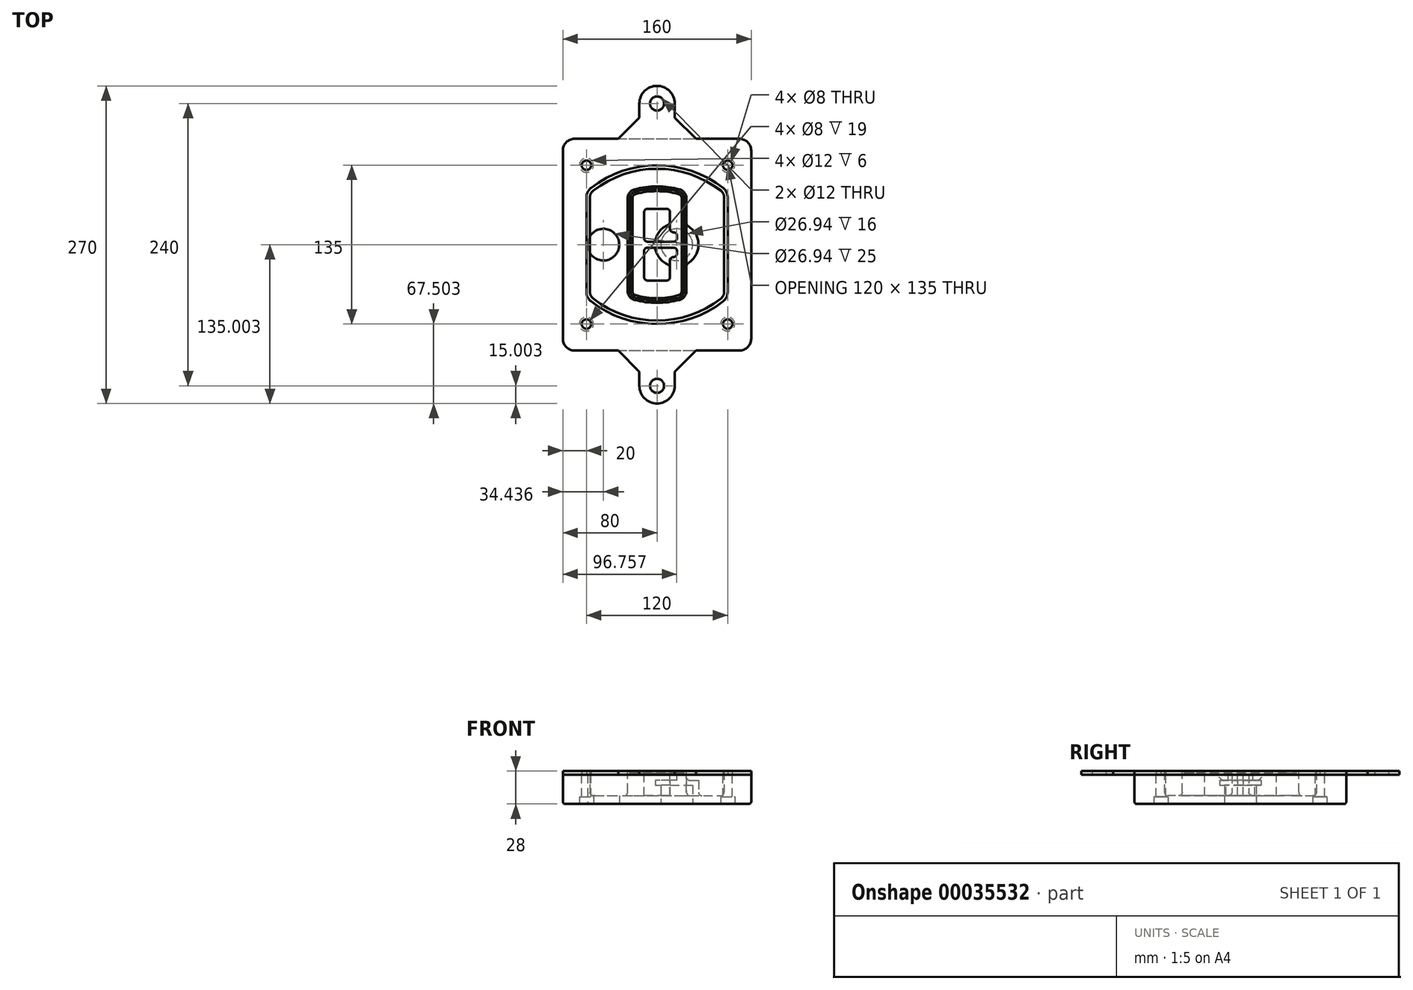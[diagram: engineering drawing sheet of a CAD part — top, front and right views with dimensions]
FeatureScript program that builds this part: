
annotation { "Feature Type Name" : "Feature", "Feature Type Description" : "" }
export const myFeature = defineFeature(function(context is Context, id is Id, definition is map)
    precondition{}
    {
        {
            var Q0;
            Q0=qCreatedBy(makeId("Top.planeOp"),FACE);
            var sketch = newSketch(context, id + "F0", { "sketchPlane" : qUnion([Q0])});
            skPoint(sketch, "E0.rect.middle", {"position": v(0, 0) * mm});
            skLineSegment(sketch, "E1.bottom", {"start": v(24.05, 28.38) * mm, "end": v(164.05, 28.38) * mm});
            skLineSegment(sketch, "E1.top", {"start": v(24.05, 208.38) * mm, "end": v(164.05, 208.38) * mm});
            skLineSegment(sketch, "E1.left", {"start": v(14.05, 38.38) * mm, "end": v(14.05, 198.38) * mm});
            skLineSegment(sketch, "E1.right", {"start": v(174.05, 38.38) * mm, "end": v(174.05, 198.38) * mm});
            skLineSegment(sketch, "E2", {"start": v(14.05, 208.38) * mm, "end": v(174.05, 28.38) * mm, "construction": true});
            skLineSegment(sketch, "E3", {"start": v(174.05, 208.38) * mm, "end": v(14.05, 28.38) * mm, "construction": true});
            skCircle(sketch, "E4", {"center": v(34.05, 185.88) * mm, "radius": 4 * mm});
            skCircle(sketch, "E5", {"center": v(154.05, 185.88) * mm, "radius": 4 * mm});
            skCircle(sketch, "E6", {"center": v(154.05, 50.88) * mm, "radius": 4 * mm});
            skCircle(sketch, "E7", {"center": v(34.05, 50.88) * mm, "radius": 4 * mm});
            skLineSegment(sketch, "E8", {"start": v(34.05, 185.88) * mm, "end": v(154.05, 185.88) * mm, "construction": true});
            skLineSegment(sketch, "E9", {"start": v(154.05, 185.88) * mm, "end": v(154.05, 50.88) * mm, "construction": true});
            skLineSegment(sketch, "E10", {"start": v(154.05, 50.88) * mm, "end": v(34.05, 50.88) * mm, "construction": true});
            skLineSegment(sketch, "E11", {"start": v(34.05, 50.88) * mm, "end": v(34.05, 185.88) * mm, "construction": true});
            skLineSegment(sketch, "E12", {"start": v(34.05, 158.68) * mm, "end": v(34.05, 78.09) * mm});
            skLineSegment(sketch, "E13", {"start": v(154.05, 158.68) * mm, "end": v(154.05, 78.09) * mm});
            skArc(sketch, "E14", {"start": v(150.2, 166.56) * mm, "mid": v(94.05, 185.88) * mm, "end": v(37.9, 166.56) * mm});
            skArc(sketch, "E15", {"start": v(37.9, 70.2) * mm, "mid": v(94.05, 50.88) * mm, "end": v(150.2, 70.2) * mm});
            skLineSegment(sketch, "E16", {"start": v(34.05, 118.38) * mm, "end": v(154.05, 118.38) * mm, "construction": true});
            skPoint(sketch, "E17.visualSharp", {"position": v(34.05, 73.38) * mm});
            skArc(sketch, "E17.filletArc", {"start": v(34.05, 78.09) * mm, "mid": v(35.06, 73.7) * mm, "end": v(37.9, 70.2) * mm});
            skPoint(sketch, "E18.visualSharp", {"position": v(34.05, 163.38) * mm});
            skArc(sketch, "E18.filletArc", {"start": v(37.9, 166.56) * mm, "mid": v(35.06, 163.06) * mm, "end": v(34.05, 158.68) * mm});
            skPoint(sketch, "E19.visualSharp", {"position": v(154.05, 163.38) * mm});
            skArc(sketch, "E19.filletArc", {"start": v(154.05, 158.68) * mm, "mid": v(153.04, 163.06) * mm, "end": v(150.2, 166.56) * mm});
            skPoint(sketch, "E20.visualSharp", {"position": v(154.05, 73.38) * mm});
            skArc(sketch, "E20.filletArc", {"start": v(150.2, 70.2) * mm, "mid": v(153.04, 73.7) * mm, "end": v(154.05, 78.09) * mm});
            skPoint(sketch, "E21.visualSharp", {"position": v(14.05, 208.38) * mm});
            skArc(sketch, "E21.filletArc", {"start": v(24.05, 208.38) * mm, "mid": v(16.98, 205.45) * mm, "end": v(14.05, 198.38) * mm});
            skPoint(sketch, "E22.visualSharp", {"position": v(174.05, 208.38) * mm});
            skArc(sketch, "E22.filletArc", {"start": v(174.05, 198.38) * mm, "mid": v(171.12, 205.45) * mm, "end": v(164.05, 208.38) * mm});
            skPoint(sketch, "E23.visualSharp", {"position": v(174.05, 28.38) * mm});
            skArc(sketch, "E23.filletArc", {"start": v(164.05, 28.38) * mm, "mid": v(171.12, 31.31) * mm, "end": v(174.05, 38.38) * mm});
            skPoint(sketch, "E24.visualSharp", {"position": v(14.05, 28.38) * mm});
            skArc(sketch, "E24.filletArc", {"start": v(14.05, 38.38) * mm, "mid": v(16.98, 31.31) * mm, "end": v(24.05, 28.38) * mm});
            skArc(sketch, "E25.0", {"start": v(151.05, 158.68) * mm, "mid": v(150.34, 161.75) * mm, "end": v(148.36, 164.2) * mm});
            skLineSegment(sketch, "E25.1", {"start": v(151.05, 158.68) * mm, "end": v(151.05, 78.09) * mm});
            skArc(sketch, "E25.2", {"start": v(148.36, 72.57) * mm, "mid": v(150.34, 75.02) * mm, "end": v(151.05, 78.09) * mm});
            skArc(sketch, "E25.3", {"start": v(39.74, 72.57) * mm, "mid": v(94.05, 53.88) * mm, "end": v(148.36, 72.57) * mm});
            skArc(sketch, "E25.4", {"start": v(37.05, 78.09) * mm, "mid": v(37.76, 75.02) * mm, "end": v(39.74, 72.57) * mm});
            skArc(sketch, "E25.5", {"start": v(148.36, 164.2) * mm, "mid": v(94.05, 182.88) * mm, "end": v(39.74, 164.2) * mm});
            skLineSegment(sketch, "E25.6", {"start": v(37.05, 158.68) * mm, "end": v(37.05, 78.09) * mm});
            skArc(sketch, "E25.7", {"start": v(39.74, 164.2) * mm, "mid": v(37.76, 161.75) * mm, "end": v(37.05, 158.68) * mm});
            skArc(sketch, "E26.0", {"start": v(35.43, 169.71) * mm, "mid": v(31.47, 164.82) * mm, "end": v(30.05, 158.68) * mm});
            skArc(sketch, "E26.1", {"start": v(152.67, 169.71) * mm, "mid": v(94.05, 189.88) * mm, "end": v(35.43, 169.71) * mm});
            skArc(sketch, "E26.2", {"start": v(158.05, 158.68) * mm, "mid": v(156.63, 164.82) * mm, "end": v(152.67, 169.71) * mm});
            skLineSegment(sketch, "E26.3", {"start": v(158.05, 158.68) * mm, "end": v(158.05, 78.09) * mm});
            skArc(sketch, "E26.4", {"start": v(152.67, 67.05) * mm, "mid": v(156.63, 71.95) * mm, "end": v(158.05, 78.09) * mm});
            skLineSegment(sketch, "E26.5", {"start": v(30.05, 158.68) * mm, "end": v(30.05, 78.09) * mm});
            skArc(sketch, "E26.6", {"start": v(35.43, 67.05) * mm, "mid": v(94.05, 46.88) * mm, "end": v(152.67, 67.05) * mm});
            skArc(sketch, "E26.7", {"start": v(30.05, 78.09) * mm, "mid": v(31.47, 71.95) * mm, "end": v(35.43, 67.05) * mm});
            skSolve(sketch);
        }
        {
            var Q0;
            Q0=makeQuery(id+"F0.imprint","IMPRINT",FACE,{"disambiguationData":[TD([[makeQuery(id+"F0.imprint","IMPRINT",EDGE,{"derivedFrom":sQuery(id+"F0.wireOp",EDGE,"E1.bottom")}),1.0]])]});
            var Q1;
            Q1=makeQuery(id+"F0.imprint","IMPRINT",FACE,{"disambiguationData":[TD([[makeQuery(id+"F0.imprint","IMPRINT",EDGE,{"derivedFrom":sQuery(id+"F0.wireOp",EDGE,"E12")}),1.0]])]});
            var Q2;
            Q2=makeQuery(id+"F0.imprint","IMPRINT",FACE,{"disambiguationData":[TD([[makeQuery(id+"F0.imprint","IMPRINT",EDGE,{"derivedFrom":sQuery(id+"F0.wireOp",EDGE,"E25.0")}),1.0]])]});
            var Q3;
            Q3=makeQuery(id+"F0.imprint","IMPRINT",FACE,{"disambiguationData":[TD([[makeQuery(id+"F0.imprint","IMPRINT",EDGE,{"derivedFrom":sQuery(id+"F0.wireOp",EDGE,"E12")}),-1.0]])]});
            extrude(context, id + "F1", {"entities" : qUnion([Q0, Q1, Q2, Q3]), "oppositeDirection" : true, "depth" : 25 * mm});
        }
        {
            var Q0;
            Q0=makeQuery(id+"F0.imprint","IMPRINT",FACE,{"disambiguationData":[TD([[makeQuery(id+"F0.imprint","IMPRINT",EDGE,{"derivedFrom":sQuery(id+"F0.wireOp",EDGE,"E12")}),1.0]])]});
            extrude(context, id + "F2", {"entities" : qUnion([Q0]), "operationType" : NewBodyOperationType.ADD, "depth" : 3 * mm});
        }
        {
            var Q0;
            Q0=makeQuery(id+"F0.imprint","IMPRINT",FACE,{"disambiguationData":[TD([[makeQuery(id+"F0.imprint","IMPRINT",EDGE,{"derivedFrom":sQuery(id+"F0.wireOp",EDGE,"E25.0")}),1.0]])]});
            extrude(context, id + "F3", {"entities" : qUnion([Q0]), "operationType" : NewBodyOperationType.REMOVE, "oppositeDirection" : true, "depth" : 18 * mm});
        }
        {
            var Q0;
            Q0=makeQuery(id+"F2.opExtrude","CAP_FACE",FACE,{"disambiguationData":[OSD([sQuery(id+"F0.wireOp",EDGE,"E12"),sQuery(id+"F0.wireOp",EDGE,"E13"),sQuery(id+"F0.wireOp",EDGE,"E14"),sQuery(id+"F0.wireOp",EDGE,"E15"),sQuery(id+"F0.wireOp",EDGE,"E17.filletArc"),sQuery(id+"F0.wireOp",EDGE,"E18.filletArc"),sQuery(id+"F0.wireOp",EDGE,"E19.filletArc"),sQuery(id+"F0.wireOp",EDGE,"E20.filletArc"),sQuery(id+"F0.wireOp",EDGE,"E25.0"),sQuery(id+"F0.wireOp",EDGE,"E25.1"),sQuery(id+"F0.wireOp",EDGE,"E25.2"),sQuery(id+"F0.wireOp",EDGE,"E25.3"),sQuery(id+"F0.wireOp",EDGE,"E25.4"),sQuery(id+"F0.wireOp",EDGE,"E25.5"),sQuery(id+"F0.wireOp",EDGE,"E25.6"),sQuery(id+"F0.wireOp",EDGE,"E25.7")])],"isStart":false});
            var sketch = newSketch(context, id + "F4", { "sketchPlane" : qUnion([Q0])});
            skArc(sketch, "E27.0", {"start": v(74.97, 71.41) * mm, "mid": v(94.05, 68.88) * mm, "end": v(113.13, 71.41) * mm});
            skArc(sketch, "E28.0", {"start": v(113.13, 165.35) * mm, "mid": v(94.05, 167.88) * mm, "end": v(74.97, 165.35) * mm});
            skLineSegment(sketch, "E29", {"start": v(69.05, 157.63) * mm, "end": v(69.05, 79.14) * mm});
            skLineSegment(sketch, "E30", {"start": v(119.05, 157.63) * mm, "end": v(119.05, 79.14) * mm});
            skLineSegment(sketch, "E31", {"start": v(69.05, 163.48) * mm, "end": v(119.05, 163.48) * mm, "construction": true});
            skLineSegment(sketch, "E32", {"start": v(69.05, 73.28) * mm, "end": v(119.05, 73.28) * mm, "construction": true});
            skPoint(sketch, "E33.visualSharp", {"position": v(69.05, 163.48) * mm});
            skArc(sketch, "E33.filletArc", {"start": v(74.97, 165.35) * mm, "mid": v(70.7, 162.5) * mm, "end": v(69.05, 157.63) * mm});
            skPoint(sketch, "E34.visualSharp", {"position": v(119.05, 163.48) * mm});
            skArc(sketch, "E34.filletArc", {"start": v(119.05, 157.63) * mm, "mid": v(117.4, 162.5) * mm, "end": v(113.13, 165.35) * mm});
            skPoint(sketch, "E35.visualSharp", {"position": v(119.05, 73.28) * mm});
            skArc(sketch, "E35.filletArc", {"start": v(113.13, 71.41) * mm, "mid": v(117.4, 74.27) * mm, "end": v(119.05, 79.14) * mm});
            skPoint(sketch, "E36.visualSharp", {"position": v(69.05, 73.28) * mm});
            skArc(sketch, "E36.filletArc", {"start": v(69.05, 79.14) * mm, "mid": v(70.7, 74.27) * mm, "end": v(74.97, 71.41) * mm});
            skArc(sketch, "E37.0", {"start": v(148.36, 164.2) * mm, "mid": v(94.05, 182.88) * mm, "end": v(39.74, 164.2) * mm});
            skArc(sketch, "E37.1", {"start": v(39.74, 164.2) * mm, "mid": v(37.76, 161.75) * mm, "end": v(37.05, 158.68) * mm});
            skLineSegment(sketch, "E37.2", {"start": v(37.05, 158.68) * mm, "end": v(37.05, 78.09) * mm});
            skArc(sketch, "E37.3", {"start": v(37.05, 78.09) * mm, "mid": v(37.76, 75.02) * mm, "end": v(39.74, 72.57) * mm});
            skArc(sketch, "E37.4", {"start": v(39.74, 72.57) * mm, "mid": v(94.05, 53.88) * mm, "end": v(148.36, 72.57) * mm});
            skArc(sketch, "E37.5", {"start": v(148.36, 72.57) * mm, "mid": v(150.34, 75.02) * mm, "end": v(151.05, 78.09) * mm});
            skLineSegment(sketch, "E37.6", {"start": v(151.05, 158.68) * mm, "end": v(151.05, 78.09) * mm});
            skArc(sketch, "E37.7", {"start": v(151.05, 158.68) * mm, "mid": v(150.34, 161.75) * mm, "end": v(148.36, 164.2) * mm});
            skLineSegment(sketch, "E38.0", {"start": v(117.05, 157.63) * mm, "end": v(117.05, 79.14) * mm});
            skArc(sketch, "E38.1", {"start": v(112.61, 73.34) * mm, "mid": v(115.81, 75.49) * mm, "end": v(117.05, 79.14) * mm});
            skArc(sketch, "E38.2", {"start": v(75.49, 73.34) * mm, "mid": v(94.05, 70.88) * mm, "end": v(112.61, 73.34) * mm});
            skArc(sketch, "E38.3", {"start": v(71.05, 79.14) * mm, "mid": v(72.29, 75.49) * mm, "end": v(75.49, 73.34) * mm});
            skLineSegment(sketch, "E38.4", {"start": v(71.05, 157.63) * mm, "end": v(71.05, 79.14) * mm});
            skArc(sketch, "E38.5", {"start": v(117.05, 157.63) * mm, "mid": v(115.81, 161.28) * mm, "end": v(112.61, 163.42) * mm});
            skArc(sketch, "E38.6", {"start": v(75.49, 163.42) * mm, "mid": v(72.29, 161.28) * mm, "end": v(71.05, 157.63) * mm});
            skArc(sketch, "E38.7", {"start": v(112.61, 163.42) * mm, "mid": v(94.05, 165.88) * mm, "end": v(75.49, 163.42) * mm});
            skArc(sketch, "E39.0", {"start": v(115.05, 157.63) * mm, "mid": v(114.23, 160.06) * mm, "end": v(112.1, 161.5) * mm});
            skLineSegment(sketch, "E39.1", {"start": v(115.05, 157.63) * mm, "end": v(115.05, 79.14) * mm});
            skArc(sketch, "E39.2", {"start": v(112.1, 75.27) * mm, "mid": v(114.23, 76.7) * mm, "end": v(115.05, 79.14) * mm});
            skArc(sketch, "E39.3", {"start": v(76, 75.27) * mm, "mid": v(94.05, 72.88) * mm, "end": v(112.1, 75.27) * mm});
            skArc(sketch, "E39.4", {"start": v(73.05, 79.14) * mm, "mid": v(73.87, 76.7) * mm, "end": v(76, 75.27) * mm});
            skArc(sketch, "E39.5", {"start": v(112.1, 161.5) * mm, "mid": v(94.05, 163.88) * mm, "end": v(76, 161.5) * mm});
            skLineSegment(sketch, "E39.6", {"start": v(73.05, 157.63) * mm, "end": v(73.05, 79.14) * mm});
            skArc(sketch, "E39.7", {"start": v(76, 161.5) * mm, "mid": v(73.87, 160.06) * mm, "end": v(73.05, 157.63) * mm});
            skLineSegment(sketch, "E40", {"start": v(69.05, 118.38) * mm, "end": v(119.05, 118.38) * mm, "construction": true});
            skLineSegment(sketch, "E41", {"start": v(83.05, 123.88) * mm, "end": v(83.05, 145.88) * mm});
            skLineSegment(sketch, "E42", {"start": v(86.05, 148.88) * mm, "end": v(102.05, 148.88) * mm});
            skLineSegment(sketch, "E43", {"start": v(105.05, 145.88) * mm, "end": v(105.05, 131.88) * mm});
            skLineSegment(sketch, "E44", {"start": v(108.05, 128.88) * mm, "end": v(108.05, 128.88) * mm});
            skLineSegment(sketch, "E45", {"start": v(111.05, 125.88) * mm, "end": v(111.05, 123.88) * mm});
            skLineSegment(sketch, "E46", {"start": v(108.05, 120.88) * mm, "end": v(86.05, 120.88) * mm});
            skPoint(sketch, "E47.visualSharp", {"position": v(83.05, 148.88) * mm});
            skArc(sketch, "E47.filletArc", {"start": v(86.05, 148.88) * mm, "mid": v(83.93, 148) * mm, "end": v(83.05, 145.88) * mm});
            skPoint(sketch, "E48.visualSharp", {"position": v(105.05, 148.88) * mm});
            skArc(sketch, "E48.filletArc", {"start": v(105.05, 145.88) * mm, "mid": v(104.17, 148) * mm, "end": v(102.05, 148.88) * mm});
            skPoint(sketch, "E49.visualSharp", {"position": v(105.05, 128.88) * mm});
            skArc(sketch, "E49.filletArc", {"start": v(105.05, 131.88) * mm, "mid": v(105.93, 129.76) * mm, "end": v(108.05, 128.88) * mm});
            skPoint(sketch, "E50.visualSharp", {"position": v(111.05, 128.88) * mm});
            skArc(sketch, "E50.filletArc", {"start": v(111.05, 125.88) * mm, "mid": v(110.17, 128) * mm, "end": v(108.05, 128.88) * mm});
            skPoint(sketch, "E51.visualSharp", {"position": v(111.05, 120.88) * mm});
            skArc(sketch, "E51.filletArc", {"start": v(108.05, 120.88) * mm, "mid": v(110.17, 121.76) * mm, "end": v(111.05, 123.88) * mm});
            skPoint(sketch, "E52.visualSharp", {"position": v(83.05, 120.88) * mm});
            skArc(sketch, "E52.filletArc", {"start": v(83.05, 123.88) * mm, "mid": v(83.93, 121.76) * mm, "end": v(86.05, 120.88) * mm});
            skLineSegment(sketch, "E53.0.MirrorCS", {"start": v(108.05, 115.88) * mm, "end": v(86.05, 115.88) * mm});
            skArc(sketch, "E54.0.MirrorCS", {"start": v(83.05, 112.88) * mm, "mid": v(83.93, 115) * mm, "end": v(86.05, 115.88) * mm});
            skLineSegment(sketch, "E55.0.MirrorCS", {"start": v(83.05, 112.88) * mm, "end": v(83.05, 90.88) * mm});
            skArc(sketch, "E56.0.MirrorCS", {"start": v(86.05, 87.88) * mm, "mid": v(83.93, 88.76) * mm, "end": v(83.05, 90.88) * mm});
            skLineSegment(sketch, "E57.0.MirrorCS", {"start": v(86.05, 87.88) * mm, "end": v(102.05, 87.88) * mm});
            skArc(sketch, "E58.0.MirrorCS", {"start": v(105.05, 90.88) * mm, "mid": v(104.17, 88.76) * mm, "end": v(102.05, 87.88) * mm});
            skLineSegment(sketch, "E59.0.MirrorCS", {"start": v(105.05, 90.88) * mm, "end": v(105.05, 104.88) * mm});
            skArc(sketch, "E60.0.MirrorCS", {"start": v(105.05, 104.88) * mm, "mid": v(105.93, 107) * mm, "end": v(108.05, 107.88) * mm});
            skArc(sketch, "E61.0.MirrorCS", {"start": v(111.05, 110.88) * mm, "mid": v(110.17, 108.76) * mm, "end": v(108.05, 107.88) * mm});
            skLineSegment(sketch, "E62.0.MirrorCS", {"start": v(111.05, 110.88) * mm, "end": v(111.05, 112.88) * mm});
            skArc(sketch, "E63.0.MirrorCS", {"start": v(108.05, 115.88) * mm, "mid": v(110.17, 115) * mm, "end": v(111.05, 112.88) * mm});
            skSolve(sketch);
        }
        {
            var Q0;
            Q0=makeQuery(id+"F4.imprint","IMPRINT",FACE,{"disambiguationData":[TD([[makeQuery(id+"F4.imprint","IMPRINT",EDGE,{"derivedFrom":sQuery(id+"F4.wireOp",EDGE,"E27.0")}),1.0]])]});
            var Q1;
            Q1=makeQuery(id+"F4.imprint","IMPRINT",FACE,{"disambiguationData":[TD([[makeQuery(id+"F4.imprint","IMPRINT",EDGE,{"derivedFrom":sQuery(id+"F4.wireOp",EDGE,"E38.0")}),-1.0]])]});
            var Q2;
            Q2=makeQuery(id+"F4.imprint","IMPRINT",FACE,{"disambiguationData":[TD([[makeQuery(id+"F4.imprint","IMPRINT",EDGE,{"derivedFrom":sQuery(id+"F4.wireOp",EDGE,"E39.0")}),1.0]])]});
            extrude(context, id + "F5", {"entities" : qUnion([Q0, Q1, Q2]), "operationType" : NewBodyOperationType.ADD, "endBound" : BoundingType.UP_TO_NEXT, "oppositeDirection" : true, "depth" : 25 * mm});
        }
        {
            var Q0;
            Q0=makeQuery(id+"F4.imprint","IMPRINT",FACE,{"disambiguationData":[TD([[makeQuery(id+"F4.imprint","IMPRINT",EDGE,{"derivedFrom":sQuery(id+"F4.wireOp",EDGE,"E38.0")}),-1.0]])]});
            extrude(context, id + "F6", {"entities" : qUnion([Q0]), "operationType" : NewBodyOperationType.REMOVE, "oppositeDirection" : true, "depth" : 2 * mm});
        }
        {
            var Q0;
            Q0=makeQuery(id+"F1.opExtrude","CAP_FACE",FACE,{"disambiguationData":[OSD([sQuery(id+"F0.wireOp",EDGE,"E1.bottom"),sQuery(id+"F0.wireOp",EDGE,"E1.top"),sQuery(id+"F0.wireOp",EDGE,"E1.left"),sQuery(id+"F0.wireOp",EDGE,"E1.right"),sQuery(id+"F0.wireOp",EDGE,"E4"),sQuery(id+"F0.wireOp",EDGE,"E5"),sQuery(id+"F0.wireOp",EDGE,"E6"),sQuery(id+"F0.wireOp",EDGE,"E7"),sQuery(id+"F0.wireOp",EDGE,"E21.filletArc"),sQuery(id+"F0.wireOp",EDGE,"E22.filletArc"),sQuery(id+"F0.wireOp",EDGE,"E23.filletArc"),sQuery(id+"F0.wireOp",EDGE,"E24.filletArc")])],"isStart":false});
            var sketch = newSketch(context, id + "F7", { "sketchPlane" : qUnion([Q0])});
            skCircle(sketch, "E64", {"center": v(110.8, -118.38) * mm, "radius": 13.47 * mm});
            skCircle(sketch, "E65", {"center": v(48.49, -118.38) * mm, "radius": 13.47 * mm});
            skLineSegment(sketch, "E66", {"start": v(174.05, -118.38) * mm, "end": v(14.05, -118.38) * mm});
            skCircle(sketch, "E67", {"center": v(110.8, -118.38) * mm, "radius": 18.47 * mm});
            skCircle(sketch, "E68", {"center": v(154.05, -185.88) * mm, "radius": 6 * mm});
            skCircle(sketch, "E69", {"center": v(34.05, -185.88) * mm, "radius": 6 * mm});
            skCircle(sketch, "E70", {"center": v(34.05, -50.88) * mm, "radius": 6 * mm});
            skCircle(sketch, "E71", {"center": v(154.05, -50.88) * mm, "radius": 6 * mm});
            skSolve(sketch);
        }
        {
            var Q0;
            {var subQ1=sQuery(id+"F7.wireOp",EDGE,"E66");var subQ4=sQuery(id+"F7.wireOp",EDGE,"E64");var subQ6=makeQuery(id+"F7.imprint","INTERSECT",VERTEX,{"disambiguationData":[OD(0.0)],"derivedFrom":[subQ4,subQ1]});Q0=makeQuery(id+"F7.imprint","IMPRINT",FACE,{"disambiguationData":[TD([[makeQuery(id+"F7.imprint","IMPRINT",EDGE,{"disambiguationData":[TD([[subQ6,-1.0]])],"derivedFrom":subQ4}),-1.0]])]});}
            var Q1;
            {var subQ0=sQuery(id+"F7.wireOp",EDGE,"E66");var subQ1=sQuery(id+"F7.wireOp",EDGE,"E64");var subQ3=makeQuery(id+"F7.imprint","INTERSECT",VERTEX,{"disambiguationData":[OD(0.0)],"derivedFrom":[subQ1,subQ0]});Q1=makeQuery(id+"F7.imprint","IMPRINT",FACE,{"disambiguationData":[TD([[makeQuery(id+"F7.imprint","IMPRINT",EDGE,{"disambiguationData":[TD([[subQ3,-1.0]])],"derivedFrom":subQ1}),1.0]])]});}
            var Q2;
            {var subQ0=sQuery(id+"F7.wireOp",EDGE,"E66");var subQ1=sQuery(id+"F7.wireOp",EDGE,"E64");var subQ3=makeQuery(id+"F7.imprint","INTERSECT",VERTEX,{"disambiguationData":[OD(0.0)],"derivedFrom":[subQ1,subQ0]});Q2=makeQuery(id+"F7.imprint","IMPRINT",FACE,{"disambiguationData":[TD([[makeQuery(id+"F7.imprint","IMPRINT",EDGE,{"disambiguationData":[TD([[subQ3,1.0]])],"derivedFrom":subQ1}),1.0]])]});}
            var Q3;
            {var subQ1=sQuery(id+"F7.wireOp",EDGE,"E66");var subQ4=sQuery(id+"F7.wireOp",EDGE,"E64");var subQ6=makeQuery(id+"F7.imprint","INTERSECT",VERTEX,{"disambiguationData":[OD(0.0)],"derivedFrom":[subQ4,subQ1]});Q3=makeQuery(id+"F7.imprint","IMPRINT",FACE,{"disambiguationData":[TD([[makeQuery(id+"F7.imprint","IMPRINT",EDGE,{"disambiguationData":[TD([[subQ6,1.0]])],"derivedFrom":subQ4}),-1.0]])]});}
            extrude(context, id + "F8", {"entities" : qUnion([Q0, Q1, Q2, Q3]), "operationType" : NewBodyOperationType.ADD, "oppositeDirection" : true, "depth" : 20 * mm});
        }
        {
            var Q0;
            {var subQ0=sQuery(id+"F7.wireOp",EDGE,"E66");var subQ1=sQuery(id+"F7.wireOp",EDGE,"E64");var subQ3=makeQuery(id+"F7.imprint","INTERSECT",VERTEX,{"disambiguationData":[OD(0.0)],"derivedFrom":[subQ1,subQ0]});Q0=makeQuery(id+"F7.imprint","IMPRINT",FACE,{"disambiguationData":[TD([[makeQuery(id+"F7.imprint","IMPRINT",EDGE,{"disambiguationData":[TD([[subQ3,-1.0]])],"derivedFrom":subQ1}),1.0]])]});}
            var Q1;
            {var subQ0=sQuery(id+"F7.wireOp",EDGE,"E66");var subQ1=sQuery(id+"F7.wireOp",EDGE,"E64");var subQ3=makeQuery(id+"F7.imprint","INTERSECT",VERTEX,{"disambiguationData":[OD(0.0)],"derivedFrom":[subQ1,subQ0]});Q1=makeQuery(id+"F7.imprint","IMPRINT",FACE,{"disambiguationData":[TD([[makeQuery(id+"F7.imprint","IMPRINT",EDGE,{"disambiguationData":[TD([[subQ3,1.0]])],"derivedFrom":subQ1}),1.0]])]});}
            extrude(context, id + "F9", {"entities" : qUnion([Q0, Q1]), "operationType" : NewBodyOperationType.REMOVE, "oppositeDirection" : true, "depth" : 16 * mm});
        }
        {
            var Q0;
            {var subQ0=sQuery(id+"F7.wireOp",EDGE,"E66");var subQ1=sQuery(id+"F7.wireOp",EDGE,"E65");var subQ3=makeQuery(id+"F7.imprint","INTERSECT",VERTEX,{"disambiguationData":[OD(0.0)],"derivedFrom":[subQ1,subQ0]});Q0=makeQuery(id+"F7.imprint","IMPRINT",FACE,{"disambiguationData":[TD([[makeQuery(id+"F7.imprint","IMPRINT",EDGE,{"disambiguationData":[TD([[subQ3,-1.0]])],"derivedFrom":subQ1}),1.0]])]});}
            var Q1;
            {var subQ0=sQuery(id+"F7.wireOp",EDGE,"E66");var subQ1=sQuery(id+"F7.wireOp",EDGE,"E65");var subQ3=makeQuery(id+"F7.imprint","INTERSECT",VERTEX,{"disambiguationData":[OD(0.0)],"derivedFrom":[subQ1,subQ0]});Q1=makeQuery(id+"F7.imprint","IMPRINT",FACE,{"disambiguationData":[TD([[makeQuery(id+"F7.imprint","IMPRINT",EDGE,{"disambiguationData":[TD([[subQ3,1.0]])],"derivedFrom":subQ1}),1.0]])]});}
            extrude(context, id + "F10", {"entities" : qUnion([Q0, Q1]), "operationType" : NewBodyOperationType.REMOVE, "oppositeDirection" : true, "depth" : 25 * mm});
        }
        {
            var Q0;
            Q0=makeQuery(id+"F7.imprint","IMPRINT",FACE,{"disambiguationData":[TD([[makeQuery(id+"F7.imprint","IMPRINT",EDGE,{"derivedFrom":sQuery(id+"F7.wireOp",EDGE,"E68")}),1.0]])]});
            var Q1;
            Q1=makeQuery(id+"F7.imprint","IMPRINT",FACE,{"disambiguationData":[TD([[makeQuery(id+"F7.imprint","IMPRINT",EDGE,{"derivedFrom":makeQuery(id+"F1.opExtrude","CAP_EDGE",EDGE,{"disambiguationData":[OSD([sQuery(id+"F0.wireOp",EDGE,"E5")])],"isStart":false})}),-1.0]])]});
            var Q2;
            Q2=makeQuery(id+"F7.imprint","IMPRINT",FACE,{"disambiguationData":[TD([[makeQuery(id+"F7.imprint","IMPRINT",EDGE,{"derivedFrom":sQuery(id+"F7.wireOp",EDGE,"E69")}),1.0]])]});
            var Q3;
            Q3=makeQuery(id+"F7.imprint","IMPRINT",FACE,{"disambiguationData":[TD([[makeQuery(id+"F7.imprint","IMPRINT",EDGE,{"derivedFrom":makeQuery(id+"F1.opExtrude","CAP_EDGE",EDGE,{"disambiguationData":[OSD([sQuery(id+"F0.wireOp",EDGE,"E4")])],"isStart":false})}),-1.0]])]});
            var Q4;
            Q4=makeQuery(id+"F7.imprint","IMPRINT",FACE,{"disambiguationData":[TD([[makeQuery(id+"F7.imprint","IMPRINT",EDGE,{"derivedFrom":sQuery(id+"F7.wireOp",EDGE,"E70")}),1.0]])]});
            var Q5;
            Q5=makeQuery(id+"F7.imprint","IMPRINT",FACE,{"disambiguationData":[TD([[makeQuery(id+"F7.imprint","IMPRINT",EDGE,{"derivedFrom":makeQuery(id+"F1.opExtrude","CAP_EDGE",EDGE,{"disambiguationData":[OSD([sQuery(id+"F0.wireOp",EDGE,"E7")])],"isStart":false})}),-1.0]])]});
            var Q6;
            Q6=makeQuery(id+"F7.imprint","IMPRINT",FACE,{"disambiguationData":[TD([[makeQuery(id+"F7.imprint","IMPRINT",EDGE,{"derivedFrom":sQuery(id+"F7.wireOp",EDGE,"E71")}),1.0]])]});
            var Q7;
            Q7=makeQuery(id+"F7.imprint","IMPRINT",FACE,{"disambiguationData":[TD([[makeQuery(id+"F7.imprint","IMPRINT",EDGE,{"derivedFrom":makeQuery(id+"F1.opExtrude","CAP_EDGE",EDGE,{"disambiguationData":[OSD([sQuery(id+"F0.wireOp",EDGE,"E6")])],"isStart":false})}),-1.0]])]});
            extrude(context, id + "F11", {"entities" : qUnion([Q0, Q1, Q2, Q3, Q4, Q5, Q6, Q7]), "operationType" : NewBodyOperationType.REMOVE, "oppositeDirection" : true, "depth" : 6 * mm});
        }
        {
            var Q0;
            Q0=makeQuery(id+"F9.boolean.opBoolean","COPY",FACE,{"derivedFrom":makeQuery(id+"F9.opExtrude","CAP_FACE",FACE,{"disambiguationData":[OSD([sQuery(id+"F7.wireOp",EDGE,"E64")])],"isStart":false})});
            var sketch = newSketch(context, id + "F12", { "sketchPlane" : qUnion([Q0])});
            skArc(sketch, "E72.0", {"start": v(105.05, -100.83) * mm, "mid": v(96.62, -106.56) * mm, "end": v(92.5, -115.88) * mm});
            skArc(sketch, "E72.1", {"start": v(92.5, -120.88) * mm, "mid": v(96.62, -130.2) * mm, "end": v(105.05, -135.93) * mm});
            skLineSegment(sketch, "E73", {"start": v(92.5, -120.88) * mm, "end": v(108.05, -120.88) * mm});
            skLineSegment(sketch, "E74.0", {"start": v(108.05, -115.88) * mm, "end": v(92.5, -115.88) * mm});
            skArc(sketch, "E74.1", {"start": v(108.05, -115.88) * mm, "mid": v(110.17, -115) * mm, "end": v(111.05, -112.88) * mm});
            skLineSegment(sketch, "E74.2", {"start": v(111.05, -110.88) * mm, "end": v(111.05, -112.88) * mm});
            skArc(sketch, "E74.3", {"start": v(111.05, -110.88) * mm, "mid": v(110.17, -108.76) * mm, "end": v(108.05, -107.88) * mm});
            skArc(sketch, "E74.4", {"start": v(105.05, -104.88) * mm, "mid": v(105.93, -107) * mm, "end": v(108.05, -107.88) * mm});
            skLineSegment(sketch, "E74.5", {"start": v(105.05, -100.83) * mm, "end": v(105.05, -104.88) * mm});
            skLineSegment(sketch, "E74.7", {"start": v(108.05, -120.88) * mm, "end": v(92.5, -120.88) * mm});
            skArc(sketch, "E74.8", {"start": v(108.05, -120.88) * mm, "mid": v(110.17, -121.76) * mm, "end": v(111.05, -123.88) * mm});
            skLineSegment(sketch, "E74.9", {"start": v(111.05, -125.88) * mm, "end": v(111.05, -123.88) * mm});
            skArc(sketch, "E74.10", {"start": v(111.05, -125.88) * mm, "mid": v(110.17, -128) * mm, "end": v(108.05, -128.88) * mm});
            skArc(sketch, "E74.11", {"start": v(105.05, -131.88) * mm, "mid": v(105.93, -129.76) * mm, "end": v(108.05, -128.88) * mm});
            skLineSegment(sketch, "E74.12", {"start": v(105.05, -135.93) * mm, "end": v(105.05, -131.88) * mm});
            skPoint(sketch, "E75.orphan", {"position": v(105.05, -145.88) * mm});
            skPoint(sketch, "E76.orphan", {"position": v(86.05, -120.88) * mm});
            skPoint(sketch, "E77.orphan", {"position": v(86.05, -115.88) * mm});
            skPoint(sketch, "E78.orphan", {"position": v(105.05, -90.88) * mm});
            skSolve(sketch);
        }
        {
            var Q0;
            {var subQ7=sQuery(id+"F12.wireOp",EDGE,"E72.0");var subQ14=sQuery(id+"F12.wireOp",EDGE,"E72.1");var subQ16=sQuery(id+"F12.wireOp",EDGE,"E74.1");var subQ18=sQuery(id+"F12.wireOp",EDGE,"E74.8");Q0=qUnion([makeQuery(id+"F12.imprint","IMPRINT",FACE,{"disambiguationData":[TD([[makeQuery(id+"F12.imprint","IMPRINT",EDGE,{"derivedFrom":subQ7}),1.0]])]}),makeQuery(id+"F12.imprint","IMPRINT",FACE,{"disambiguationData":[TD([[makeQuery(id+"F12.imprint","IMPRINT",EDGE,{"derivedFrom":subQ14}),1.0]])]}),makeQuery(id+"F12.imprint","IMPRINT",FACE,{"disambiguationData":[TD([[makeQuery(id+"F12.imprint","IMPRINT",EDGE,{"derivedFrom":subQ16}),1.0]])]}),makeQuery(id+"F12.imprint","IMPRINT",FACE,{"disambiguationData":[TD([[makeQuery(id+"F12.imprint","IMPRINT",EDGE,{"derivedFrom":subQ18}),-1.0]])]})]);}
            var Q1;
            Q1=makeQuery(id+"F5.boolean.opBoolean","SPLIT",FACE,{"disambiguationData":[TD([makeQuery(id+"F5.opExtrude","SWEPT_FACE",FACE,{"disambiguationData":[OSD([sQuery(id+"F4.wireOp",EDGE,"E41")])]})])],"derivedFrom":makeQuery(id+"F3.boolean.opBoolean","COPY",FACE,{"derivedFrom":makeQuery(id+"F3.opExtrude","CAP_FACE",FACE,{"disambiguationData":[OSD([sQuery(id+"F0.wireOp",EDGE,"E25.0"),sQuery(id+"F0.wireOp",EDGE,"E25.1"),sQuery(id+"F0.wireOp",EDGE,"E25.2"),sQuery(id+"F0.wireOp",EDGE,"E25.3"),sQuery(id+"F0.wireOp",EDGE,"E25.4"),sQuery(id+"F0.wireOp",EDGE,"E25.5"),sQuery(id+"F0.wireOp",EDGE,"E25.6"),sQuery(id+"F0.wireOp",EDGE,"E25.7")])],"isStart":false})})});
            extrude(context, id + "F13", {"entities" : qUnion([Q0]), "operationType" : NewBodyOperationType.REMOVE, "endBound" : BoundingType.UP_TO_SURFACE, "endBoundEntityFace" : qUnion([Q1]), "depth" : 25 * mm});
        }
        {
            var Q0;
            Q0=makeQuery(id+"F3.boolean.opBoolean","COPY",EDGE,{"derivedFrom":makeQuery(id+"F3.opExtrude","CAP_EDGE",EDGE,{"disambiguationData":[OSD([sQuery(id+"F0.wireOp",EDGE,"E25.6")])],"isStart":false})});
            var Q1;
            Q1=makeQuery(id+"F8.boolean.opBoolean","INTERSECT",EDGE,{"derivedFrom":[makeQuery(id+"F5.opExtrude","SWEPT_FACE",FACE,{"disambiguationData":[OSD([sQuery(id+"F4.wireOp",EDGE,"E30")])]}),makeQuery(id+"F8.opExtrude","CAP_FACE",FACE,{"disambiguationData":[OSD([sQuery(id+"F7.wireOp",EDGE,"E67")])],"isStart":false})]});
            var Q2;
            Q2=makeQuery(id+"F8.boolean.opBoolean","INTERSECT",EDGE,{"disambiguationData":[OD(1.0)],"derivedFrom":[makeQuery(id+"F5.opExtrude","SWEPT_FACE",FACE,{"disambiguationData":[OSD([sQuery(id+"F4.wireOp",EDGE,"E30")])]}),makeQuery(id+"F8.opExtrude","SWEPT_FACE",FACE,{"disambiguationData":[OSD([sQuery(id+"F7.wireOp",EDGE,"E67")])]})]});
            var Q3;
            {var subQ0=sQuery(id+"F4.wireOp",EDGE,"E30");Q3=makeQuery(id+"F8.boolean.opBoolean","SPLIT",EDGE,{"disambiguationData":[TD([makeQuery(id+"F5.opExtrude","SWEPT_FACE",FACE,{"disambiguationData":[OSD([sQuery(id+"F4.wireOp",EDGE,"E35.filletArc")])]})])],"derivedFrom":makeQuery(id+"F5.opExtrude","CAP_EDGE",EDGE,{"disambiguationData":[OSD([subQ0])],"isStart":false})});}
            var Q4;
            {var subQ0=sQuery(id+"F0.wireOp",EDGE,"E25.7");var subQ1=sQuery(id+"F0.wireOp",EDGE,"E25.1");var subQ2=sQuery(id+"F0.wireOp",EDGE,"E25.6");var subQ3=sQuery(id+"F0.wireOp",EDGE,"E25.5");var subQ4=sQuery(id+"F0.wireOp",EDGE,"E25.4");var subQ5=sQuery(id+"F0.wireOp",EDGE,"E25.0");var subQ6=sQuery(id+"F0.wireOp",EDGE,"E25.2");var subQ7=sQuery(id+"F0.wireOp",EDGE,"E25.3");Q4=makeQuery(id+"F8.boolean.opBoolean","INTERSECT",EDGE,{"derivedFrom":[makeQuery(id+"F5.boolean.opBoolean","SPLIT",FACE,{"disambiguationData":[TD([makeQuery(id+"F2.opExtrude","SWEPT_FACE",FACE,{"disambiguationData":[OSD([subQ5])]})])],"derivedFrom":makeQuery(id+"F3.boolean.opBoolean","COPY",FACE,{"derivedFrom":makeQuery(id+"F3.opExtrude","CAP_FACE",FACE,{"disambiguationData":[OSD([subQ5,subQ1,subQ6,subQ7,subQ4,subQ3,subQ2,subQ0])],"isStart":false})})}),makeQuery(id+"F8.opExtrude","SWEPT_FACE",FACE,{"disambiguationData":[OSD([sQuery(id+"F7.wireOp",EDGE,"E67")])]})]});}
            var Q5;
            Q5=makeQuery(id+"F8.boolean.opBoolean","INTERSECT",EDGE,{"disambiguationData":[OD(0.0)],"derivedFrom":[makeQuery(id+"F5.opExtrude","SWEPT_FACE",FACE,{"disambiguationData":[OSD([sQuery(id+"F4.wireOp",EDGE,"E30")])]}),makeQuery(id+"F8.opExtrude","SWEPT_FACE",FACE,{"disambiguationData":[OSD([sQuery(id+"F7.wireOp",EDGE,"E67")])]})]});
            fillet(context, id + "F14", {"entities" : qUnion([Q0, Q1, Q2, Q3, Q4, Q5]), "radius" : 3 * mm, "tangentPropagation" : true, "allowEdgeOverflow" : false});
        }
        {
            var Q0;
            Q0=makeQuery(id+"F1.opExtrude","CAP_EDGE",EDGE,{"disambiguationData":[OSD([sQuery(id+"F0.wireOp",EDGE,"E1.bottom")])],"isStart":false});
            fillet(context, id + "F15", {"entities" : qUnion([Q0]), "radius" : 2 * mm, "tangentPropagation" : true, "allowEdgeOverflow" : false});
        }
        {
            var Q0;
            {var subQ0=sQuery(id+"F0.wireOp",EDGE,"E1.bottom");var subQ1=sQuery(id+"F0.wireOp",EDGE,"E1.top");var subQ2=sQuery(id+"F0.wireOp",EDGE,"E1.left");var subQ3=sQuery(id+"F0.wireOp",EDGE,"E1.right");var subQ4=sQuery(id+"F0.wireOp",EDGE,"E4");var subQ5=sQuery(id+"F0.wireOp",EDGE,"E5");var subQ6=sQuery(id+"F0.wireOp",EDGE,"E6");var subQ7=sQuery(id+"F0.wireOp",EDGE,"E7");var subQ8=sQuery(id+"F0.wireOp",EDGE,"E21.filletArc");var subQ9=sQuery(id+"F0.wireOp",EDGE,"E22.filletArc");var subQ10=sQuery(id+"F0.wireOp",EDGE,"E23.filletArc");var subQ11=sQuery(id+"F0.wireOp",EDGE,"E24.filletArc");Q0=makeQuery(id+"F2.boolean.opBoolean","SPLIT",FACE,{"disambiguationData":[TD([makeQuery(id+"F1.opExtrude","SWEPT_FACE",FACE,{"disambiguationData":[OSD([subQ0])]})])],"derivedFrom":makeQuery(id+"F1.opExtrude","CAP_FACE",FACE,{"disambiguationData":[OSD([subQ0,subQ1,subQ2,subQ3,subQ4,subQ5,subQ6,subQ7,subQ8,subQ9,subQ10,subQ11])],"isStart":true})});}
            var sketch = newSketch(context, id + "F16", { "sketchPlane" : qUnion([Q0])});
            skLineSegment(sketch, "E79", {"start": v(94.05, 208.38) * mm, "end": v(94.05, 238.38) * mm, "construction": true});
            skCircle(sketch, "E80", {"center": v(94.05, 238.38) * mm, "radius": 6 * mm});
            skArc(sketch, "E81", {"start": v(109.05, 238.38) * mm, "mid": v(94.05, 253.38) * mm, "end": v(79.05, 238.38) * mm});
            skLineSegment(sketch, "E82", {"start": v(79.05, 238.38) * mm, "end": v(79.05, 226.38) * mm});
            skLineSegment(sketch, "E83", {"start": v(79.05, 226.38) * mm, "end": v(61.05, 208.38) * mm});
            skLineSegment(sketch, "E84", {"start": v(109.05, 238.38) * mm, "end": v(109.05, 226.38) * mm});
            skLineSegment(sketch, "E85", {"start": v(109.05, 226.38) * mm, "end": v(127.05, 208.38) * mm});
            skLineSegment(sketch, "E86", {"start": v(14.05, 118.38) * mm, "end": v(174.05, 118.38) * mm, "construction": true});
            skLineSegment(sketch, "E87.MirrorCS", {"start": v(79.05, 10.38) * mm, "end": v(61.05, 28.38) * mm});
            skLineSegment(sketch, "E88.MirrorCS", {"start": v(79.05, -1.62) * mm, "end": v(79.05, 10.38) * mm});
            skArc(sketch, "E89.MirrorCS", {"start": v(109.05, -1.62) * mm, "mid": v(94.05, -16.62) * mm, "end": v(79.05, -1.62) * mm});
            skCircle(sketch, "E90.MirrorC", {"center": v(94.05, -1.62) * mm, "radius": 6 * mm});
            skLineSegment(sketch, "E91.MirrorCS", {"start": v(109.05, -1.62) * mm, "end": v(109.05, 10.38) * mm});
            skLineSegment(sketch, "E92.MirrorCS", {"start": v(109.05, 10.38) * mm, "end": v(127.05, 28.38) * mm});
            skSolve(sketch);
        }
        {
            var Q0;
            Q0=makeQuery(id+"F16.imprint","IMPRINT",FACE,{"disambiguationData":[TD([[makeQuery(id+"F16.imprint","IMPRINT",EDGE,{"derivedFrom":sQuery(id+"F16.wireOp",EDGE,"E80")}),-1.0]])]});
            var Q1;
            Q1=makeQuery(id+"F16.imprint","IMPRINT",FACE,{"disambiguationData":[TD([[makeQuery(id+"F16.imprint","IMPRINT",EDGE,{"derivedFrom":makeQuery(id+"F1.opExtrude","CAP_EDGE",EDGE,{"disambiguationData":[OSD([sQuery(id+"F0.wireOp",EDGE,"E1.left")])],"isStart":true})}),-1.0]])]});
            var Q2;
            {var subQ2=sQuery(id+"F16.wireOp",EDGE,"E87.MirrorCS");Q2=makeQuery(id+"F16.imprint","IMPRINT",FACE,{"disambiguationData":[TD([[makeQuery(id+"F16.imprint","IMPRINT",EDGE,{"derivedFrom":subQ2}),-1.0]])]});}
            var Q3;
            Q3=makeQuery(id+"F2.opExtrude","CAP_FACE",FACE,{"disambiguationData":[OSD([sQuery(id+"F0.wireOp",EDGE,"E12"),sQuery(id+"F0.wireOp",EDGE,"E13"),sQuery(id+"F0.wireOp",EDGE,"E14"),sQuery(id+"F0.wireOp",EDGE,"E15"),sQuery(id+"F0.wireOp",EDGE,"E17.filletArc"),sQuery(id+"F0.wireOp",EDGE,"E18.filletArc"),sQuery(id+"F0.wireOp",EDGE,"E19.filletArc"),sQuery(id+"F0.wireOp",EDGE,"E20.filletArc"),sQuery(id+"F0.wireOp",EDGE,"E25.0"),sQuery(id+"F0.wireOp",EDGE,"E25.1"),sQuery(id+"F0.wireOp",EDGE,"E25.2"),sQuery(id+"F0.wireOp",EDGE,"E25.3"),sQuery(id+"F0.wireOp",EDGE,"E25.4"),sQuery(id+"F0.wireOp",EDGE,"E25.5"),sQuery(id+"F0.wireOp",EDGE,"E25.6"),sQuery(id+"F0.wireOp",EDGE,"E25.7")])],"isStart":false});
            extrude(context, id + "F17", {"entities" : qUnion([Q0, Q1, Q2]), "endBound" : BoundingType.UP_TO_SURFACE, "endBoundEntityFace" : qUnion([Q3]), "depth" : 25 * mm});
        }
    });
